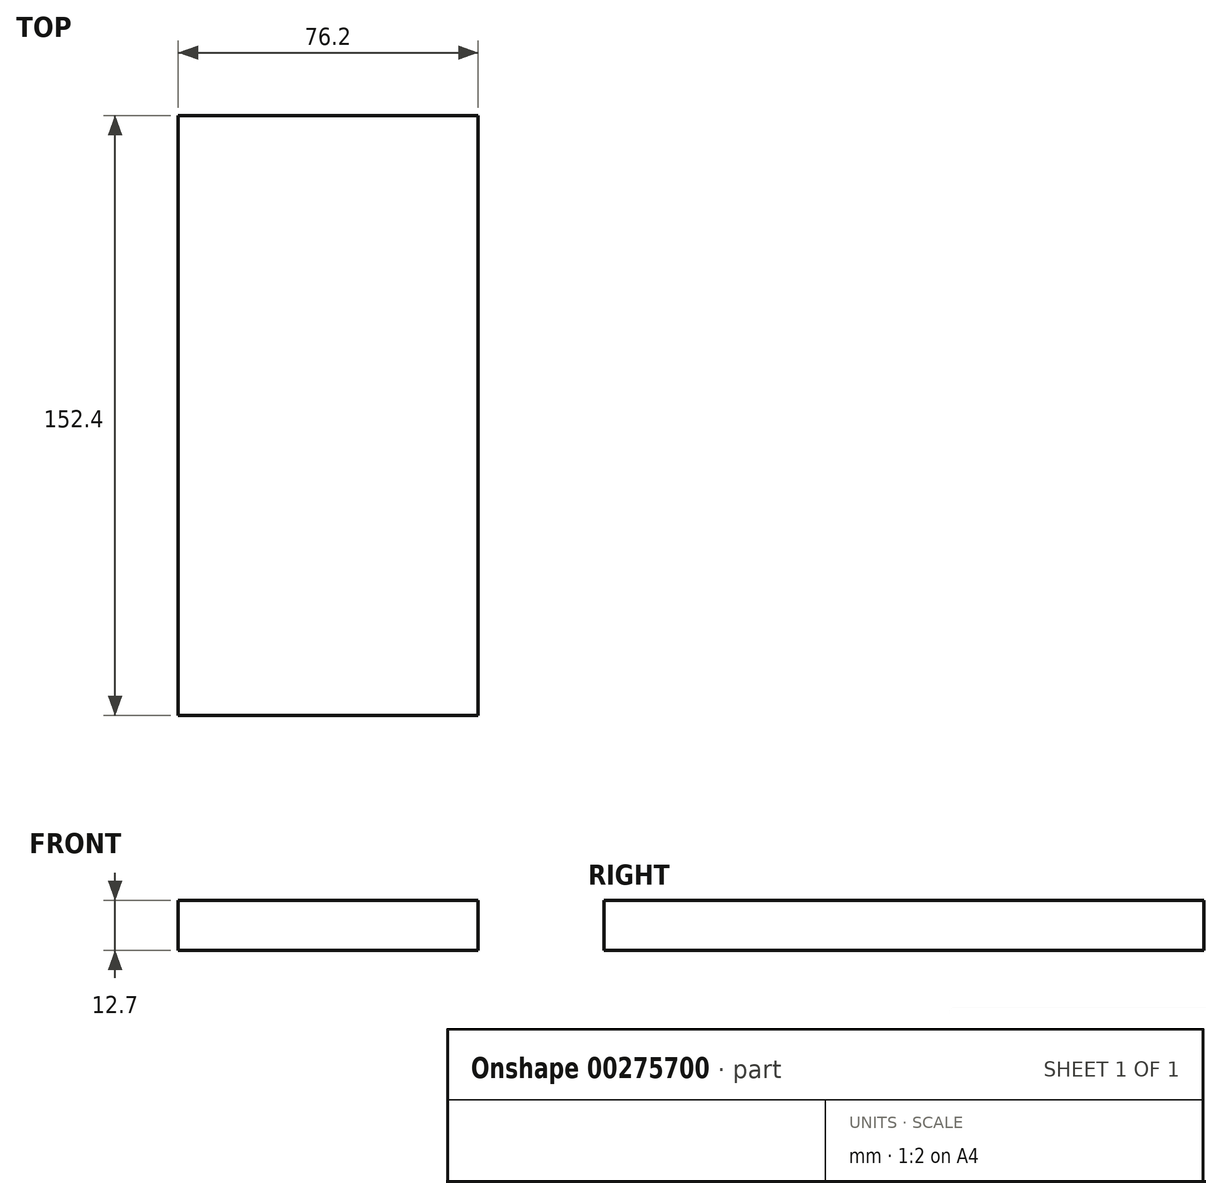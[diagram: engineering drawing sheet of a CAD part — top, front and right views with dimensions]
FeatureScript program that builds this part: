
annotation { "Feature Type Name" : "Feature", "Feature Type Description" : "" }
export const myFeature = defineFeature(function(context is Context, id is Id, definition is map)
    precondition{}
    {
        {
            var Q0;
            Q0=qCreatedBy(makeId("Front.planeOp"),FACE);
            var sketch = newSketch(context, id + "F0", { "sketchPlane" : qUnion([Q0])});
            skLineSegment(sketch, "E0.bottom", {"start": v(-124.63, -21.38) * mm, "end": v(-48.43, -21.38) * mm});
            skLineSegment(sketch, "E0.top", {"start": v(-124.63, -34.08) * mm, "end": v(-48.43, -34.08) * mm});
            skLineSegment(sketch, "E0.left", {"start": v(-124.63, -21.38) * mm, "end": v(-124.63, -34.08) * mm});
            skLineSegment(sketch, "E0.right", {"start": v(-48.43, -21.38) * mm, "end": v(-48.43, -34.08) * mm});
            skSolve(sketch);
        }
        {
            var Q0;
            Q0=makeQuery(id+"F0.imprint","IMPRINT",FACE,{"disambiguationData":[TD([[makeQuery(id+"F0.imprint","IMPRINT",EDGE,{"derivedFrom":sQuery(id+"F0.wireOp",EDGE,"E0.bottom")}),-1.0]])]});
            extrude(context, id + "F1", {"entities" : qUnion([Q0]), "depth" : 152.4 * mm});
        }
    });
